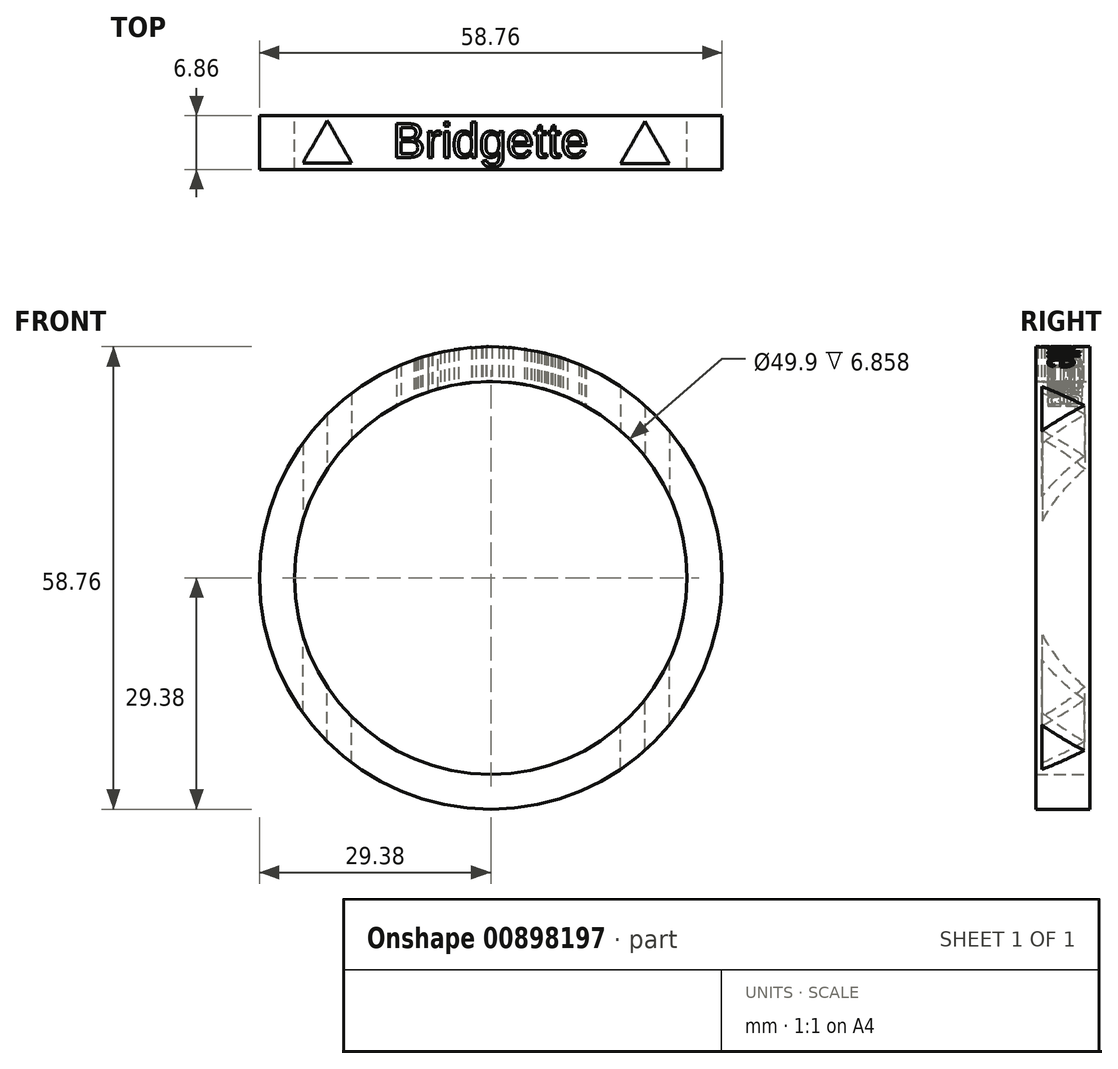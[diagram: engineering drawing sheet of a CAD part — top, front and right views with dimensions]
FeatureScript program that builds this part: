
annotation { "Feature Type Name" : "Feature", "Feature Type Description" : "" }
export const myFeature = defineFeature(function(context is Context, id is Id, definition is map)
    precondition{}
    {
        {
            var Q0;
            Q0=qCreatedBy(makeId("Front.planeOp"),FACE);
            var sketch = newSketch(context, id + "F0", { "sketchPlane" : qUnion([Q0])});
            skCircle(sketch, "E0", {"center": v(0, 0) * mm, "radius": 29.38 * mm});
            skCircle(sketch, "E1", {"center": v(0, 0) * mm, "radius": 24.95 * mm});
            skSolve(sketch);
        }
        {
            var Q0;
            Q0 = qSketchRegion(id + "F0", true);
            extrude(context, id + "F1", {"entities" : qUnion([Q0]), "depth" : 6.86 * mm, "offsetDistance" : 25.4 * mm});
        }
        {
            var Q0;
            Q0=qCreatedBy(makeId("Top.planeOp"),FACE);
            var sketch = newSketch(context, id + "F2", { "sketchPlane" : qUnion([Q0])});
            skText(sketch, "E2", { "text": "Bridgette", "fontName": "Arimo-Regular.ttf"});
            const initialGuessF2  = {"E2": [-0.0125, -0.0053, 1, 0, 0.00447]};
            skSetInitialGuess(sketch, initialGuessF2);
            skSolve(sketch);
        }
        {
            var Q0;
            Q0 = qSketchRegion(id + "F2", true);
            extrude(context, id + "F3", {"entities" : qUnion([Q0]), "operationType" : NewBodyOperationType.REMOVE, "depth" : 52.07 * mm, "offsetDistance" : 25.4 * mm});
        }
        {
            var Q0;
            Q0=qCreatedBy(makeId("Top.planeOp"),FACE);
            var sketch = newSketch(context, id + "F4", { "sketchPlane" : qUnion([Q0])});
            skLineSegment(sketch, "E3.0", {"start": v(22.7, -6.12) * mm, "end": v(16.46, -6.12) * mm});
            skLineSegment(sketch, "E3.1", {"start": v(16.46, -6.12) * mm, "end": v(19.58, -0.72) * mm});
            skLineSegment(sketch, "E3.2", {"start": v(19.58, -0.72) * mm, "end": v(22.7, -6.12) * mm});
            skPoint(sketch, "E3.0.midPoint", {"position": v(19.58, -6.12) * mm});
            skLineSegment(sketch, "E4.0", {"start": v(-17.66, -6.03) * mm, "end": v(-23.87, -6.03) * mm});
            skLineSegment(sketch, "E4.1", {"start": v(-23.87, -6.03) * mm, "end": v(-20.76, -0.64) * mm});
            skLineSegment(sketch, "E4.2", {"start": v(-20.76, -0.64) * mm, "end": v(-17.66, -6.03) * mm});
            skPoint(sketch, "E5.startSnap0", {"position": v(-22.32, -3.34) * mm});
            skPoint(sketch, "E5.start.orphan", {"position": v(-20.86, -3.34) * mm});
            skPoint(sketch, "E6.end.orphan", {"position": v(-20.76, -3.17) * mm});
            skSolve(sketch);
        }
        {
            var Q0;
            Q0 = qSketchRegion(id + "F4", true);
            extrude(context, id + "F5", {"entities" : qUnion([Q0]), "operationType" : NewBodyOperationType.REMOVE, "depth" : 25.4 * mm, "offsetDistance" : 25.4 * mm});
        }
        {
            var Q0;
            Q0 = qSketchRegion(id + "F4", true);
            extrude(context, id + "F6", {"entities" : qUnion([Q0]), "operationType" : NewBodyOperationType.REMOVE, "oppositeDirection" : true, "depth" : 25.4 * mm, "offsetDistance" : 25.4 * mm});
        }
    });
